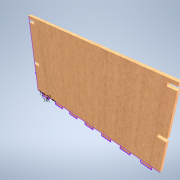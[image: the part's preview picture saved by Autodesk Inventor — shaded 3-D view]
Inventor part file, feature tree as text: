
AUTODESK INVENTOR PART (.ipt)
format: ipt  version: 2021 (Build 250183000, 183)  size: 187,392 bytes
history: native  units: mm
features: extrude x3, sketch x3, other x1
ambient origin geometry x8: Origin, YZ Plane, XZ Plane, XY Plane, X Axis, Y Axis, Z Axis, Center Point
bodies: Solid1 (feature_tree)
feature tree (7):
  other  "DoosjeVoor-Achterkant"
  extrude  "Extrusion1"  Depth=77.0mm
  extrude  "Extrusion2"  Depth=3.0mm
  extrude  "Extrusion3"  Depth=70.0mm
  sketch  "Sketch1"  dims[d0=144.0mm d1=77.0mm]
  sketch  "Sketch2"  dims[d2=3.0mm d3=0.0mm d4=3.0mm]
  sketch  "Sketch3"  dims[d5=10.0mm d6=70.0mm d8=20.0mm d9=10.0mm d11=10.0mm d25=3.0mm d26=0.0mm d27=7.0mm d28=3.0mm d29=20.0mm d31=137.0mm d32=20.0mm d34=41.0mm d37=0.0mm d38=0.0mm]
